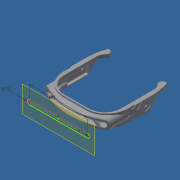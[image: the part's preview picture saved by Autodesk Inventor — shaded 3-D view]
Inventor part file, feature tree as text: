
AUTODESK INVENTOR PART (.ipt)
format: ipt  version: 2014 (Build 180170000, 170)  size: 1,284,096 bytes
history: native  units: in
note: dims shown in document units (in); Inventor stores cm internally (conversion verified against a paired STEP export)
features: fillet x18, sketch x17, extrude x16, mirror x3, plane x3, loft x1, hole x1, projected_geometry x1
ambient origin geometry x8: Origin, YZ Plane, XZ Plane, XY Plane, X Axis, Y Axis, Z Axis, Center Point
bodies: Solid1 (feature_tree)
feature tree (60):
  extrude  "Extrusion1"  Depth=5.5118in
  fillet  "Fillet1"  Radius=7.0866in
  fillet  "Fillet2"  Radius=7.0866in
  sketch  "Sketch2"  dims[d29=1.1811in d30=0.0in d31=1.5748in d32=0.7874in]
  extrude  "Extrusion2"  Depth=1.5748in
  fillet  "Fillet3"  Radius=0.7874in
  mirror  "Mirror1"
  extrude  "Extrusion3"  Depth=0.3937in
  fillet  "Fillet4"  Radius=0.315in
  fillet  "Fillet5"  Radius=0.1969in
  extrude  "Extrusion4"  Depth=1.9685in
  sketch  "Sketch5"  dims[d42=0.3937in d43=0.0in d44=0.3543in]
  extrude  "Extrusion5"  Depth=0.3937in
  plane  "Work Plane1"
  loft  "Loft1"
  extrude  "Extrusion6"  Depth=5.3543in
  extrude  "Extrusion7"  Depth=0.3937in TaperAngle=0.0deg
  fillet  "Fillet6"  Radius=0.7874in
  fillet  "Fillet7"  Radius=0.4724in
  extrude  "Extrusion8"  TaperAngle=0.0deg  [1 undecoded]
  extrude  "Extrusion9"  Depth=0.1181in
  hole  "Hole1"  [1 undecoded]
  mirror  "Mirror2"
  extrude  "Extrusion10"  Depth=0.3937in TaperAngle=0.0deg
  plane  "Work Plane2"
  extrude  "Extrusion11"  Depth=0.1181in
  sketch  "Sketch13"  dims[d69=1.1811in d70=0.1181in]
  extrude  "Extrusion12"  Depth=0.8661in
  extrude  "Extrusion13"  Depth=0.5118in
  extrude  "Extrusion14"  Depth=0.3937in TaperAngle=0.0deg
  fillet  "Fillet8"  Radius=0.8268in
  fillet  "Fillet9"  Radius=0.3937in
  fillet  "Fillet10"  Radius=0.5906in
  extrude  "Extrusion15"  Depth=0.3937in
  fillet  "Fillet11"  Radius=0.0787in
  fillet  "Fillet12"  Radius=2.0472in
  fillet  "Fillet13"  Radius=0.9567in
  fillet  "Fillet14"  Radius=0.1122in
  fillet  "Fillet15"  Radius=0.0394in
  fillet  "Fillet16"  Radius=0.2559in
  mirror  "Mirror3"
  extrude  "Extrusion16"  Depth=1.9685in
  fillet  "Fillet17"  Radius=0.5796in
  fillet  "Fillet18"  Radius=0.4724in
  plane  "Work Plane3"
  sketch  "Sketch17"  dims[d81=0.0591in d82=0.0in d83=0.3937in d84=0.3937in d85=0.2559in d86=0.2362in d87=0.1575in d88=0.0787in d89=90.0deg d90=0.315in d91=0.0in d92=0.0787in d93=2.0472in d94=0.9567in d95=0.1122in d96=0.0394in d97=0.2559in d98=0.0in d99=0.5796in d100=0.5796in d101=0.0in d102=0.4724in d103=0.9055in d104=0.1969in d105=0.4528in d106=0.2756in d107=0.0in d108=0.1181in d109=0.0in d110=0.3937in d111=0.2756in d112=0.0in d113=0.0197in d114=0.1378in d115=0.0787in d116=0.2756in d117=0.0in d118=0.1181in d119=0.1181in d120=0.0197in d121=0.0197in d122=0.0197in d123=0.0197in d124=0.1575in d125=0.2756in d126=0.0in d127=0.1575in d128=1.9685in d129=1.5748in d130=0.4331in d131=5.5118in d132=0.2165in]
  sketch  "Sketch1"  dims[d0=5.5118in d1=5.5118in d21=7.0866in d22=7.0866in]
  sketch  "Sketch3"  dims[d33=0.3937in d34=0.1378in d37=0.315in d38=0.1969in]
  sketch  "Sketch4"  dims[d39=1.1811in d40=0.0in d41=1.9685in]
  sketch  "Sketch6"  dims[d45=5.9055in d46=0.3937in d47=0.0in]
  sketch  "Sketch7"  dims[d48=0.9449in d49=5.3543in]
  sketch  "Sketch8"  dims[d52=0.5906in d53=0.3937in d54=0.0in d55=0.7874in d56=0.4724in]
  sketch  "Sketch9"  dims[d57=0.0in d58=90.0deg d59=0.0in d60=90.0deg]
  sketch  "Sketch10"  dims[d61=0.2756in d62=0.1181in]
  sketch  "Sketch11"  dims[d63=0.3436in d64=2.7953in d65=0.0in]
  sketch  "Sketch12"  dims[d66=6.2205in d67=0.3937in d68=0.0in]
  sketch  "Sketch14"  dims[d71=1.5748in d72=0.8661in]
  projected_geometry  "Projected Loop1"
  sketch  "Sketch15"  dims[d73=0.2756in d74=0.5118in]
  sketch  "Sketch16"  dims[d75=0.0787in d76=0.0787in d77=0.0in d78=0.8268in d79=0.3937in d80=0.5906in]
note: 2 required parameter values undecoded (feature->parameter linkage not recoverable at this tier; creation-order binding heuristic only, values carry confidence <= 0.55)
